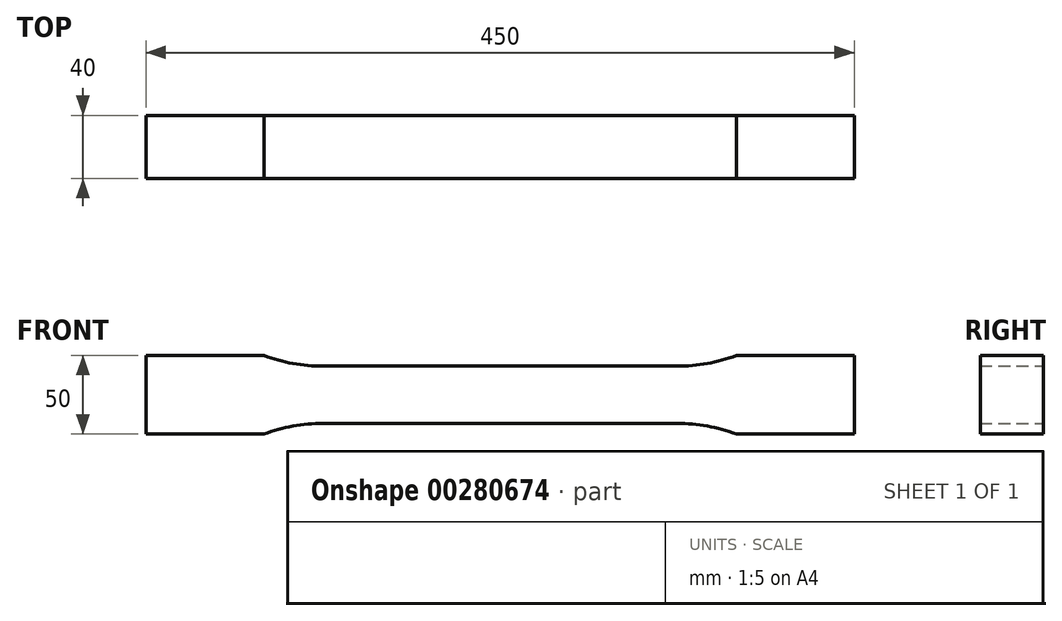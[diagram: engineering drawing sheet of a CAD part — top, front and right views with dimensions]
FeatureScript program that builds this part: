
annotation { "Feature Type Name" : "Feature", "Feature Type Description" : "" }
export const myFeature = defineFeature(function(context is Context, id is Id, definition is map)
    precondition{}
    {
        {
            var Q0;
            Q0=qCreatedBy(makeId("Front.planeOp"),FACE);
            var sketch = newSketch(context, id + "F0", { "sketchPlane" : qUnion([Q0])});
            skLineSegment(sketch, "E0", {"start": v(0, 18.16) * mm, "end": v(112.5, 18.16) * mm});
            skArc(sketch, "E1", {"start": v(112.5, 18.16) * mm, "mid": v(131.56, 19.89) * mm, "end": v(150, 25) * mm});
            skLineSegment(sketch, "E2", {"start": v(150, 25) * mm, "end": v(225, 25) * mm});
            skLineSegment(sketch, "E3", {"start": v(225, 25) * mm, "end": v(225, 0) * mm});
            skArc(sketch, "E4.MirrorCS", {"start": v(112.5, -18.16) * mm, "mid": v(131.56, -19.89) * mm, "end": v(150, -25) * mm});
            skLineSegment(sketch, "E5.MirrorCS", {"start": v(150, -25) * mm, "end": v(225, -25) * mm});
            skLineSegment(sketch, "E6.MirrorCS", {"start": v(225, -25) * mm, "end": v(225, 0) * mm});
            skLineSegment(sketch, "E7.MirrorCS", {"start": v(0, -18.16) * mm, "end": v(112.5, -18.16) * mm});
            skLineSegment(sketch, "E8.MirrorCS", {"start": v(0, 18.16) * mm, "end": v(-112.5, 18.16) * mm});
            skLineSegment(sketch, "E9.MirrorCS", {"start": v(0, -18.16) * mm, "end": v(-112.5, -18.16) * mm});
            skArc(sketch, "E10.MirrorCS", {"start": v(-112.5, -18.16) * mm, "mid": v(-131.56, -19.89) * mm, "end": v(-150, -25) * mm});
            skLineSegment(sketch, "E11.MirrorCS", {"start": v(-225, -25) * mm, "end": v(-225, 0) * mm});
            skLineSegment(sketch, "E12.MirrorCS", {"start": v(-225, 25) * mm, "end": v(-225, 0) * mm});
            skLineSegment(sketch, "E13.MirrorCS", {"start": v(-150, -25) * mm, "end": v(-225, -25) * mm});
            skLineSegment(sketch, "E14.MirrorCS", {"start": v(-150, 25) * mm, "end": v(-225, 25) * mm});
            skArc(sketch, "E15.MirrorCS", {"start": v(-112.5, 18.16) * mm, "mid": v(-131.56, 19.89) * mm, "end": v(-150, 25) * mm});
            skSolve(sketch);
        }
        {
            var Q0;
            Q0 = qSketchRegion(id + "F0", true);
            extrude(context, id + "F1", {"entities" : qUnion([Q0]), "endBound" : BoundingType.SYMMETRIC, "depth" : 40 * mm});
        }
    });
